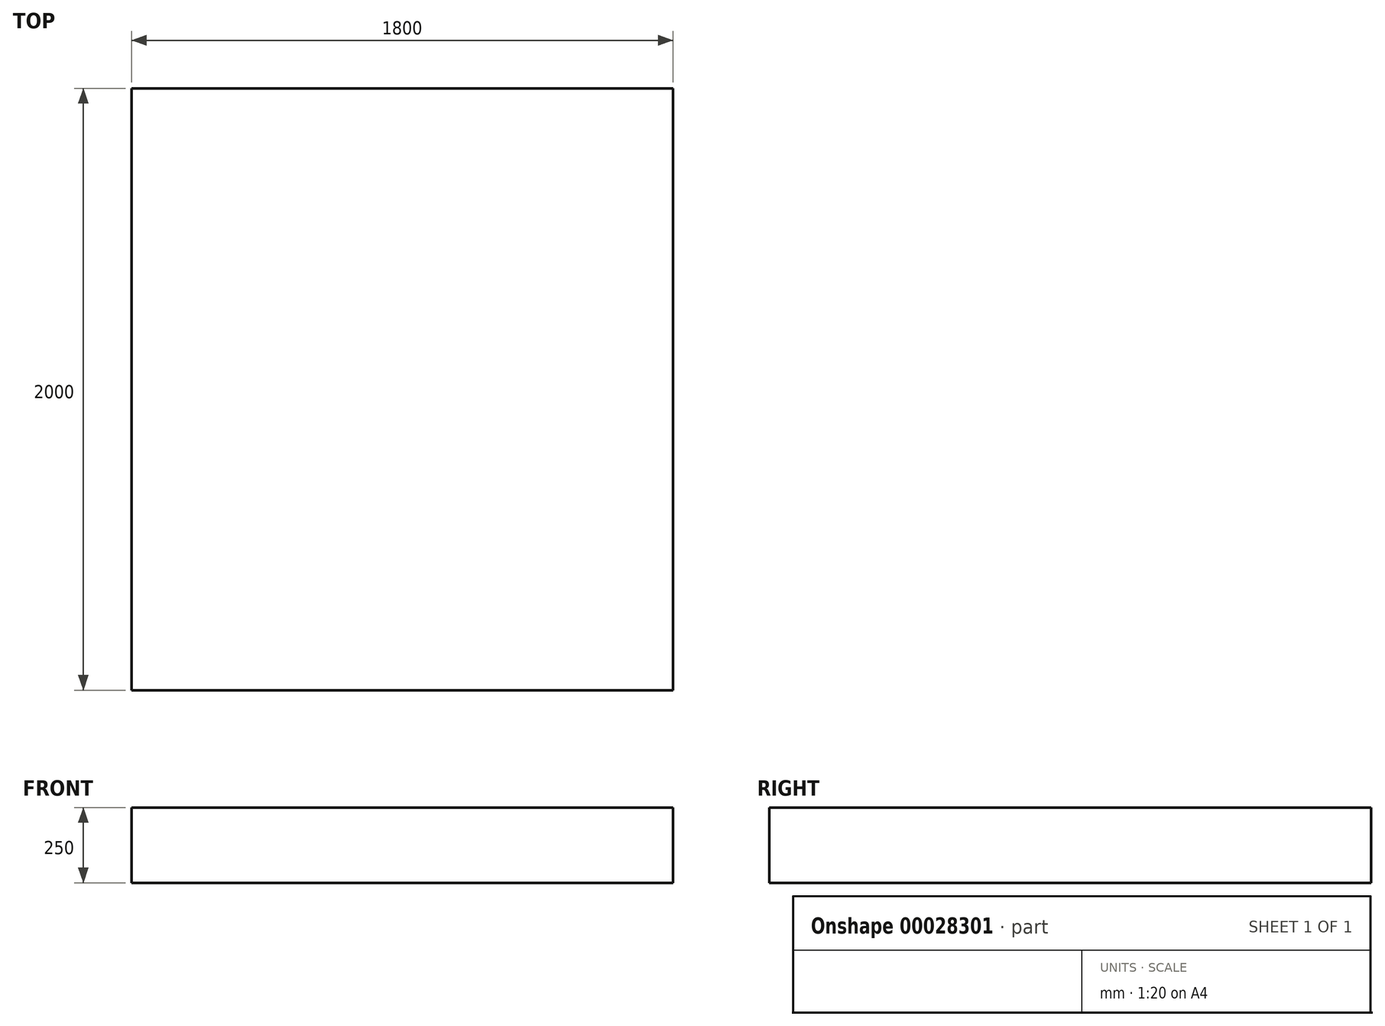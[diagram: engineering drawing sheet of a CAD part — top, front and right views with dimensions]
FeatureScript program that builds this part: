
annotation { "Feature Type Name" : "Feature", "Feature Type Description" : "" }
export const myFeature = defineFeature(function(context is Context, id is Id, definition is map)
    precondition{}
    {
        {
            var Q0;
            Q0=qCreatedBy(makeId("Top.planeOp"),FACE);
            var sketch = newSketch(context, id + "F0", { "sketchPlane" : qUnion([Q0])});
            skLineSegment(sketch, "E0", {"start": v(0, 0) * mm, "end": v(1800, 0) * mm});
            skLineSegment(sketch, "E1", {"start": v(1800, 0) * mm, "end": v(1800, 2000) * mm});
            skLineSegment(sketch, "E2", {"start": v(1800, 2000) * mm, "end": v(0, 2000) * mm});
            skLineSegment(sketch, "E3", {"start": v(0, 2000) * mm, "end": v(0, 0) * mm});
            skSolve(sketch);
        }
        {
            var Q0;
            Q0 = qSketchRegion(id + "F0", true);
            extrude(context, id + "F1", {"entities" : qUnion([Q0]), "depth" : 250 * mm});
        }
    });
